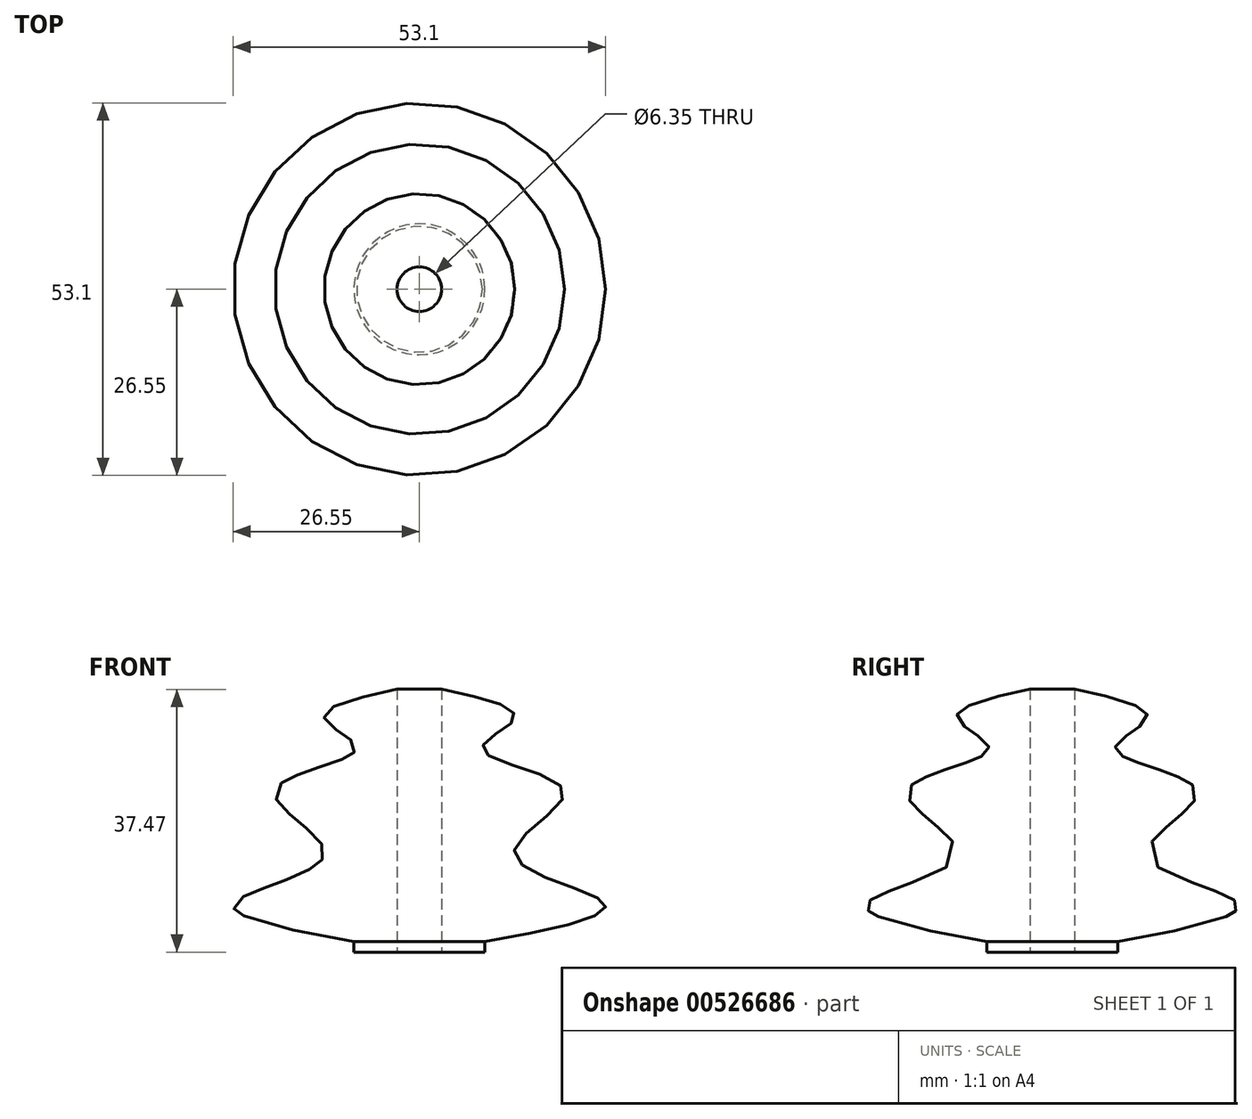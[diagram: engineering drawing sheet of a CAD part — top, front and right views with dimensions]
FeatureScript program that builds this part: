
annotation { "Feature Type Name" : "Feature", "Feature Type Description" : "" }
export const myFeature = defineFeature(function(context is Context, id is Id, definition is map)
    precondition{}
    {
        {
            var Q0;
            Q0=qCreatedBy(makeId("Front.planeOp"),FACE);
            var sketch = newSketch(context, id + "F0", { "sketchPlane" : qUnion([Q0])});
            skFitSpline(sketch, "E0", {"points": [v(0, 0) * mm, v(26.28, 7.13) * mm, v(13.51, 14.08) * mm, v(20.65, 22.9) * mm, v(9, 28.9) * mm, v(13.51, 33.22) * mm, v(0, 38.1) * mm], "startDerivative": vector(184.04, 29.43) * mm, "endDerivative": vector(-128.2, 25.02) * mm});
            skLineSegment(sketch, "E1", {"start": v(0, 38.1) * mm, "end": v(0, 0) * mm});
            skSolve(sketch);
        }
        {
            var Q0;
            Q0=makeQuery(id+"F0.imprint","IMPRINT",FACE,{"disambiguationData":[TD([[makeQuery(id+"F0.imprint","IMPRINT",EDGE,{"derivedFrom":sQuery(id+"F0.wireOp",EDGE,"E0")}),1.0]])]});
            var Q1;
            Q1=sQuery(id+"F0.wireOp",EDGE,"E1");
            revolve(context, id + "F1", {"entities" : qUnion([Q0]), "axis" : qUnion([Q1]), "revolveType" : RevolveType.FULL});
        }
        {
            var Q0;
            Q0=qCreatedBy(makeId("Top.planeOp"),FACE);
            var sketch = newSketch(context, id + "F2", { "sketchPlane" : qUnion([Q0])});
            skCircle(sketch, "E2", {"center": v(0, 0) * mm, "radius": 9.34 * mm});
            skSolve(sketch);
        }
        {
            var Q0;
            Q0=makeQuery(id+"F2.imprint","IMPRINT",FACE,{"disambiguationData":[TD([[makeQuery(id+"F2.imprint","IMPRINT",EDGE,{"derivedFrom":sQuery(id+"F2.wireOp",EDGE,"E2")}),1.0]])]});
            extrude(context, id + "F3", {"entities" : qUnion([Q0]), "operationType" : NewBodyOperationType.ADD, "depth" : 12.7 * mm, "offsetDistance" : 25.4 * mm});
        }
        {
            var Q0;
            Q0=qCreatedBy(makeId("Top.planeOp"),FACE);
            var sketch = newSketch(context, id + "F4", { "sketchPlane" : qUnion([Q0])});
            skCircle(sketch, "E3.cCircle", {"center": v(0, 0) * mm, "radius": 4.32 * mm, "construction": true});
            skLineSegment(sketch, "E3.0", {"start": v(-2.08, 4.32) * mm, "end": v(2.08, 4.32) * mm});
            skLineSegment(sketch, "E3.1", {"start": v(2.08, 4.32) * mm, "end": v(4.67, 1.07) * mm});
            skLineSegment(sketch, "E3.2", {"start": v(4.67, 1.07) * mm, "end": v(3.75, -2.99) * mm});
            skLineSegment(sketch, "E3.3", {"start": v(3.75, -2.99) * mm, "end": v(0, -4.8) * mm});
            skLineSegment(sketch, "E3.4", {"start": v(0, -4.8) * mm, "end": v(-3.75, -2.99) * mm});
            skLineSegment(sketch, "E3.5", {"start": v(-3.75, -2.99) * mm, "end": v(-4.67, 1.07) * mm});
            skLineSegment(sketch, "E3.6", {"start": v(-4.67, 1.07) * mm, "end": v(-2.08, 4.32) * mm});
            skPoint(sketch, "E3.0.midPoint", {"position": v(0, 4.32) * mm});
            skSolve(sketch);
        }
        {
            var Q0;
            Q0=sQuery(id+"F4.wireOp",VERTEX,"E3.cCircle.center");
            var Q1;
            Q1=makeQuery(id+"F1.opRevolve","SWEPT_BODY",BODY,{"disambiguationData":[OSD([sQuery(id+"F0.wireOp",EDGE,"E0"),sQuery(id+"F0.wireOp",EDGE,"E1")])]});
            hole(context, id + "F5", {"style" : HoleStyle.SIMPLE, "endStyle" : HoleEndStyle.THROUGH, "oppositeDirection" : true, "holeDiameter" : 6.35 * mm, "isTappedThrough" : true, "tappedDepth" : 12.7 * mm, "tapClearance" : 3, "locations" : qUnion([Q0]), "scope" : qUnion([Q1])});
        }
    });
